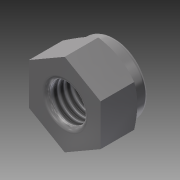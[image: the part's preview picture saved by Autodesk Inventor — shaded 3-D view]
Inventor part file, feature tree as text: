
AUTODESK INVENTOR PART (.ipt)
format: ipt  version: 2013 (Build 170138000, 138)  size: 180,224 bytes
history: native  units: mm
features: sketch x3, extrude x2, fillet x2, other x1, revolve x1, thread x1
ambient origin geometry x1: Origin
feature tree (10):
  other  "ソリッド1"
  revolve  "回転1"
  extrude  "押し出し2"  Depth=4.5mm
  fillet  "フィレット1"  [1 undecoded]
  extrude  "押し出し3"  Depth=2.75mm
  fillet  "フィレット2"  Radius=5.5mm
  thread  "ねじ3"
  sketch  "スケッチ1"
  sketch  "スケッチ3"
  sketch  "スケッチ4"
note: 1 required parameter value undecoded (feature->parameter linkage not recoverable at this tier; creation-order binding heuristic only, values carry confidence <= 0.55)
